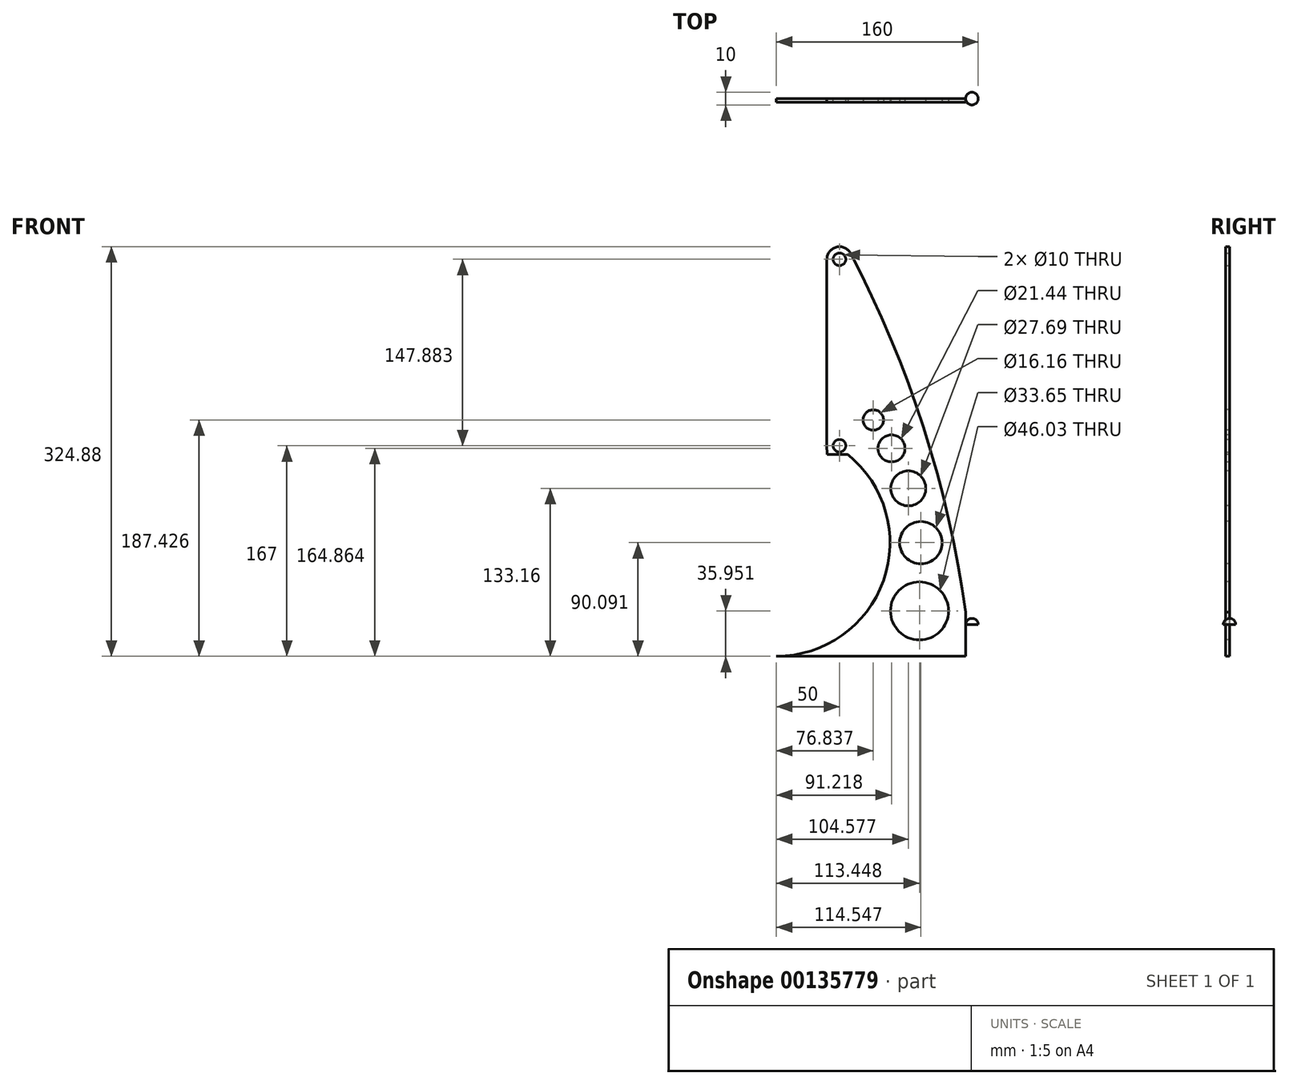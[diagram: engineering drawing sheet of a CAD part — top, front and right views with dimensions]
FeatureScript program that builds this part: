
annotation { "Feature Type Name" : "Feature", "Feature Type Description" : "" }
export const myFeature = defineFeature(function(context is Context, id is Id, definition is map)
    precondition{}
    {
        {
            var Q0;
            Q0=qCreatedBy(makeId("Front.planeOp"),FACE);
            var sketch = newSketch(context, id + "F0", { "sketchPlane" : qUnion([Q0])});
            skLineSegment(sketch, "E0.bottom", {"start": v(0, 0) * mm, "end": v(-150, 0) * mm});
            skLineSegment(sketch, "E0.top", {"start": v(0, 10) * mm, "end": v(-150, 10) * mm});
            skLineSegment(sketch, "E0.left", {"start": v(0, 0) * mm, "end": v(0, 10) * mm});
            skLineSegment(sketch, "E0.right", {"start": v(-150, 0) * mm, "end": v(-150, 10) * mm});
            skLineSegment(sketch, "E1", {"start": v(-100, 0) * mm, "end": v(-100, 289.88) * mm, "construction": true});
            skPoint(sketch, "E2", {"position": v(-100, 289.88) * mm});
            skPoint(sketch, "E3", {"position": v(-100, 0) * mm});
            skPoint(sketch, "E4", {"position": v(-100, 142) * mm});
            skCircle(sketch, "E5", {"center": v(-100, 142) * mm, "radius": 5 * mm});
            skCircle(sketch, "E6", {"center": v(-100, 289.88) * mm, "radius": 5 * mm});
            skCircle(sketch, "E7", {"center": v(-100, 142) * mm, "radius": 10 * mm});
            skCircle(sketch, "E8", {"center": v(-100, 289.88) * mm, "radius": 10 * mm});
            skPoint(sketch, "E9", {"position": v(-100, 80) * mm});
            skArc(sketch, "E10", {"start": v(-150, 10) * mm, "mid": v(-107.22, 32.3) * mm, "end": v(-100, 80) * mm});
            skArc(sketch, "E11", {"start": v(-110, 142) * mm, "mid": v(-107.48, 110.6) * mm, "end": v(-100, 80) * mm});
            skArc(sketch, "E12", {"start": v(0, 10) * mm, "mid": v(-33.27, 156.2) * mm, "end": v(-91.14, 294.52) * mm});
            skLineSegment(sketch, "E13", {"start": v(-110, 142) * mm, "end": v(-110, 289.88) * mm});
            skLineSegment(sketch, "E14.bottom", {"start": v(-150, 0) * mm, "end": v(0, 0) * mm});
            skLineSegment(sketch, "E14.top", {"start": v(-150, -25) * mm, "end": v(0, -25) * mm});
            skLineSegment(sketch, "E14.left", {"start": v(-150, 0) * mm, "end": v(-150, -25) * mm});
            skLineSegment(sketch, "E14.right", {"start": v(0, 0) * mm, "end": v(0, -25) * mm});
            skSolve(sketch);
        }
        {
            var Q0;
            Q0 = qSketchRegion(id + "F0", true);
            extrude(context, id + "F1", {"entities" : qUnion([Q0]), "depth" : 3 * mm});
        }
        {
            var Q0;
            Q0=makeQuery(id+"F1.opExtrude","CAP_FACE",FACE,{"disambiguationData":[OSD([sQuery(id+"F0.wireOp",EDGE,"E0.left"),sQuery(id+"F0.wireOp",EDGE,"E0.right"),sQuery(id+"F0.wireOp",EDGE,"E5"),sQuery(id+"F0.wireOp",EDGE,"E6"),sQuery(id+"F0.wireOp",EDGE,"E8"),sQuery(id+"F0.wireOp",EDGE,"E10"),sQuery(id+"F0.wireOp",EDGE,"E11"),sQuery(id+"F0.wireOp",EDGE,"E12"),sQuery(id+"F0.wireOp",EDGE,"E13"),sQuery(id+"F0.wireOp",EDGE,"E14.top"),sQuery(id+"F0.wireOp",EDGE,"E14.left"),sQuery(id+"F0.wireOp",EDGE,"E14.right")])],"isStart":false});
            var sketch = newSketch(context, id + "F2", { "sketchPlane" : qUnion([Q0])});
            skLineSegment(sketch, "E15", {"start": v(0, 0) * mm, "end": v(-110, 142) * mm});
            skArc(sketch, "E16", {"start": v(-110, 142) * mm, "mid": v(-79.28, 52.19) * mm, "end": v(0, 0) * mm});
            skArc(sketch, "E17", {"start": v(-150, -25) * mm, "mid": v(-97.66, -1.97) * mm, "end": v(-79.28, 52.19) * mm});
            skSolve(sketch);
        }
        {
            var Q0;
            {var subQ0=sQuery(id+"F2.wireOp",EDGE,"E17");Q0=makeQuery(id+"F2.imprint","IMPRINT",FACE,{"disambiguationData":[TD([[makeQuery(id+"F2.imprint","IMPRINT",EDGE,{"derivedFrom":subQ0}),1.0]])]});}
            extrude(context, id + "F3", {"entities" : qUnion([Q0]), "operationType" : NewBodyOperationType.REMOVE, "oppositeDirection" : true, "depth" : 25 * mm});
        }
        {
            var Q0;
            Q0=makeQuery(id+"F1.opExtrude","CAP_FACE",FACE,{"disambiguationData":[OSD([sQuery(id+"F0.wireOp",EDGE,"E0.left"),sQuery(id+"F0.wireOp",EDGE,"E0.right"),sQuery(id+"F0.wireOp",EDGE,"E5"),sQuery(id+"F0.wireOp",EDGE,"E6"),sQuery(id+"F0.wireOp",EDGE,"E8"),sQuery(id+"F0.wireOp",EDGE,"E10"),sQuery(id+"F0.wireOp",EDGE,"E11"),sQuery(id+"F0.wireOp",EDGE,"E12"),sQuery(id+"F0.wireOp",EDGE,"E13"),sQuery(id+"F0.wireOp",EDGE,"E14.top"),sQuery(id+"F0.wireOp",EDGE,"E14.left"),sQuery(id+"F0.wireOp",EDGE,"E14.right")])],"isStart":false});
            var sketch = newSketch(context, id + "F4", { "sketchPlane" : qUnion([Q0])});
            skLineSegment(sketch, "E18", {"start": v(-109.83, 135) * mm, "end": v(-93.43, 135) * mm});
            skArc(sketch, "E19", {"start": v(-150, -25) * mm, "mid": v(-65.15, 35) * mm, "end": v(-93.43, 135) * mm});
            skSolve(sketch);
        }
        {
            var Q0;
            {var subQ0=sQuery(id+"F4.wireOp",EDGE,"E18");Q0=makeQuery(id+"F4.imprint","IMPRINT",FACE,{"disambiguationData":[TD([[makeQuery(id+"F4.imprint","IMPRINT",EDGE,{"derivedFrom":subQ0}),-1.0]])]});}
            extrude(context, id + "F5", {"entities" : qUnion([Q0]), "operationType" : NewBodyOperationType.REMOVE, "oppositeDirection" : true, "depth" : 25 * mm});
        }
        {
            var Q0;
            Q0=qCreatedBy(makeId("Front.planeOp"),FACE);
            var sketch = newSketch(context, id + "F6", { "sketchPlane" : qUnion([Q0])});
            skLineSegment(sketch, "E20", {"start": v(0, 0) * mm, "end": v(10, 0) * mm});
            skArc(sketch, "E21", {"start": v(10, 0) * mm, "mid": v(5, 5) * mm, "end": v(0, 0) * mm});
            skLineSegment(sketch, "E22", {"start": v(5, 0) * mm, "end": v(5, 11.96) * mm, "construction": true});
            skLineSegment(sketch, "E23", {"start": v(5, 0) * mm, "end": v(5, 5) * mm});
            skSolve(sketch);
        }
        {
            var Q0;
            {var subQ3=sQuery(id+"F6.wireOp",EDGE,"E23");Q0=makeQuery(id+"F6.imprint","IMPRINT",FACE,{"disambiguationData":[TD([[makeQuery(id+"F6.imprint","IMPRINT",EDGE,{"derivedFrom":subQ3}),1.0]])]});}
            var Q1;
            Q1=sQuery(id+"F6.wireOp",EDGE,"E22");
            revolve(context, id + "F7", {"entities" : qUnion([Q0]), "axis" : qUnion([Q1]), "revolveType" : RevolveType.FULL});
        }
        {
            var Q0;
            Q0=makeQuery(id+"F1.opExtrude","CAP_FACE",FACE,{"disambiguationData":[OSD([sQuery(id+"F0.wireOp",EDGE,"E0.left"),sQuery(id+"F0.wireOp",EDGE,"E0.right"),sQuery(id+"F0.wireOp",EDGE,"E5"),sQuery(id+"F0.wireOp",EDGE,"E6"),sQuery(id+"F0.wireOp",EDGE,"E8"),sQuery(id+"F0.wireOp",EDGE,"E10"),sQuery(id+"F0.wireOp",EDGE,"E11"),sQuery(id+"F0.wireOp",EDGE,"E12"),sQuery(id+"F0.wireOp",EDGE,"E13"),sQuery(id+"F0.wireOp",EDGE,"E14.top"),sQuery(id+"F0.wireOp",EDGE,"E14.left"),sQuery(id+"F0.wireOp",EDGE,"E14.right")])],"isStart":false});
            var sketch = newSketch(context, id + "F8", { "sketchPlane" : qUnion([Q0])});
            skCircle(sketch, "E24", {"center": v(-36.55, 10.95) * mm, "radius": 23.02 * mm});
            skCircle(sketch, "E25", {"center": v(-35.45, 65.1) * mm, "radius": 16.82 * mm});
            skCircle(sketch, "E26", {"center": v(-45.42, 108.16) * mm, "radius": 13.85 * mm});
            skCircle(sketch, "E27", {"center": v(-58.78, 139.86) * mm, "radius": 10.72 * mm});
            skCircle(sketch, "E28", {"center": v(-73.16, 162.43) * mm, "radius": 8.08 * mm});
            skSolve(sketch);
        }
        {
            var Q0;
            Q0=makeQuery(id+"F8.imprint","IMPRINT",FACE,{"disambiguationData":[TD([[makeQuery(id+"F8.imprint","IMPRINT",EDGE,{"derivedFrom":sQuery(id+"F8.wireOp",EDGE,"E27")}),1.0]])]});
            var Q1;
            Q1=makeQuery(id+"F8.imprint","IMPRINT",FACE,{"disambiguationData":[TD([[makeQuery(id+"F8.imprint","IMPRINT",EDGE,{"derivedFrom":sQuery(id+"F8.wireOp",EDGE,"E26")}),1.0]])]});
            var Q2;
            Q2=makeQuery(id+"F8.imprint","IMPRINT",FACE,{"disambiguationData":[TD([[makeQuery(id+"F8.imprint","IMPRINT",EDGE,{"derivedFrom":sQuery(id+"F8.wireOp",EDGE,"E28")}),1.0]])]});
            var Q3;
            Q3=makeQuery(id+"F8.imprint","IMPRINT",FACE,{"disambiguationData":[TD([[makeQuery(id+"F8.imprint","IMPRINT",EDGE,{"derivedFrom":sQuery(id+"F8.wireOp",EDGE,"E25")}),1.0]])]});
            var Q4;
            Q4=makeQuery(id+"F8.imprint","IMPRINT",FACE,{"disambiguationData":[TD([[makeQuery(id+"F8.imprint","IMPRINT",EDGE,{"derivedFrom":sQuery(id+"F8.wireOp",EDGE,"E24")}),1.0]])]});
            extrude(context, id + "F9", {"entities" : qUnion([Q0, Q1, Q2, Q3, Q4]), "operationType" : NewBodyOperationType.REMOVE, "oppositeDirection" : true, "depth" : 25 * mm});
        }
    });
